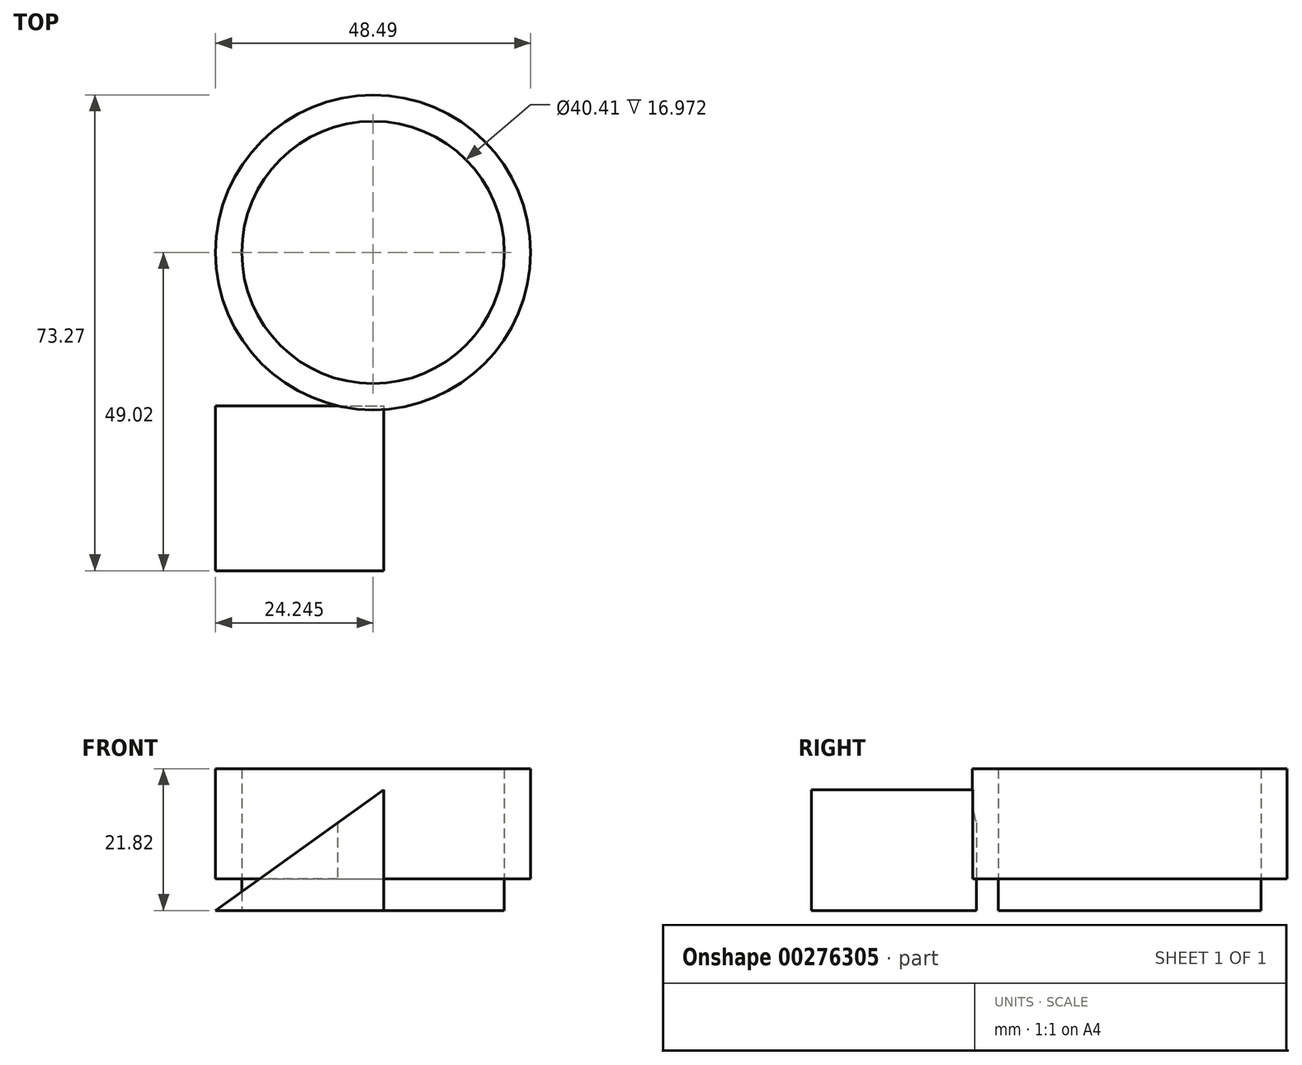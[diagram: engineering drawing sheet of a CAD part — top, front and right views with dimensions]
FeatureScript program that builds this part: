
annotation { "Feature Type Name" : "Feature", "Feature Type Description" : "" }
export const myFeature = defineFeature(function(context is Context, id is Id, definition is map)
    precondition{}
    {
        {
            var Q0;
            Q0=qCreatedBy(makeId("Front.planeOp"),FACE);
            var sketch = newSketch(context, id + "F0", { "sketchPlane" : qUnion([Q0])});
            skLineSegment(sketch, "E0.bottom", {"start": v(0, 0) * mm, "end": v(4.04, 0) * mm});
            skLineSegment(sketch, "E0.top", {"start": v(0, 21.82) * mm, "end": v(4.04, 21.82) * mm});
            skLineSegment(sketch, "E0.left", {"start": v(0, 0) * mm, "end": v(0, 21.82) * mm});
            skLineSegment(sketch, "E0.right", {"start": v(4.04, 0) * mm, "end": v(4.04, 21.82) * mm});
            skLineSegment(sketch, "E1.bottom", {"start": v(0, 0) * mm, "end": v(24.25, 0) * mm});
            skLineSegment(sketch, "E1.top", {"start": v(0, 4.85) * mm, "end": v(24.25, 4.85) * mm});
            skLineSegment(sketch, "E1.left", {"start": v(0, 0) * mm, "end": v(0, 4.85) * mm});
            skLineSegment(sketch, "E1.right", {"start": v(24.25, 0) * mm, "end": v(24.25, 4.85) * mm});
            skSolve(sketch);
        }
        {
            var Q0;
            {var subQ0=sQuery(id+"F0.wireOp",EDGE,"E0.top");Q0=makeQuery(id+"F0.imprint","IMPRINT",FACE,{"disambiguationData":[TD([[makeQuery(id+"F0.imprint","IMPRINT",EDGE,{"derivedFrom":subQ0}),-1.0]])]});}
            var Q1;
            {var subQ5=sQuery(id+"F0.wireOp",EDGE,"E1.left");Q1=makeQuery(id+"F0.imprint","IMPRINT",FACE,{"disambiguationData":[TD([[makeQuery(id+"F0.imprint","IMPRINT",EDGE,{"derivedFrom":subQ5}),-1.0]])]});}
            var Q2;
            {var subQ5=sQuery(id+"F0.wireOp",EDGE,"E1.right");Q2=makeQuery(id+"F0.imprint","IMPRINT",FACE,{"disambiguationData":[TD([[makeQuery(id+"F0.imprint","IMPRINT",EDGE,{"derivedFrom":subQ5}),1.0]])]});}
            var Q3;
            Q3=sQuery(id+"F0.wireOp",EDGE,"E1.right");
            revolve(context, id + "F1", {"entities" : qUnion([Q0, Q1, Q2]), "axis" : qUnion([Q3]), "revolveType" : RevolveType.FULL});
        }
        {
            var Q0;
            Q0=qCreatedBy(makeId("Front.planeOp"),FACE);
            cPlane(context, id + "F2", {"entities" : qUnion([Q0]), "cplaneType" : CPlaneType.OFFSET, "offset" : 23.62 * mm, "width" : 152.4 * mm, "height" : 152.4 * mm});
        }
        {
            var Q0;
            Q0=qCreatedBy(id+"F2.planeOp",FACE);
            var sketch = newSketch(context, id + "F3", { "sketchPlane" : qUnion([Q0])});
            skLineSegment(sketch, "E2", {"start": v(0, 0) * mm, "end": v(25.86, 0) * mm});
            skLineSegment(sketch, "E3", {"start": v(25.86, 0) * mm, "end": v(25.86, 18.59) * mm});
            skLineSegment(sketch, "E4", {"start": v(25.86, 18.59) * mm, "end": v(0, 0) * mm});
            skSolve(sketch);
        }
        {
            var Q0;
            Q0=makeQuery(id+"F3.imprint","IMPRINT",FACE,{"disambiguationData":[TD([[makeQuery(id+"F3.imprint","IMPRINT",EDGE,{"derivedFrom":sQuery(id+"F3.wireOp",EDGE,"E2")}),1.0]])]});
            extrude(context, id + "F4", {"entities" : qUnion([Q0]), "operationType" : NewBodyOperationType.ADD, "depth" : 25.4 * mm});
        }
    });
